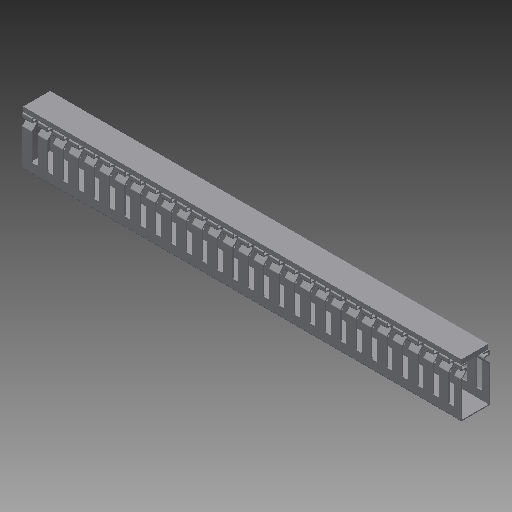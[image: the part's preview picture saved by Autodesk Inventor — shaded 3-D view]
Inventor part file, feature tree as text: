
AUTODESK INVENTOR PART (.ipt)
format: ipt  version: 2017 (Build 210142000, 142)  size: 1,247,232 bytes
history: native  units: in
note: dims shown in document units (in); Inventor stores cm internally (conversion verified against a paired STEP export)
features: other x1, extrude x1, imported_body x1, sketch x1
ambient origin geometry x8: Origin, YZ Plane, XZ Plane, XY Plane, X Axis, Y Axis, Z Axis, Center Point
bodies: Solid1 (feature_tree)
feature tree (4):
  other  "User Library-PVC Wire Duct 30x50x455.SAT1"
  extrude  "Extrusión1"  [1 undecoded]
  imported_body  "Base1"
  sketch  "Boceto2"  dims[d1=0.1969in d2=0.0in]
note: 1 required parameter value undecoded (feature->parameter linkage not recoverable at this tier; creation-order binding heuristic only, values carry confidence <= 0.55)
